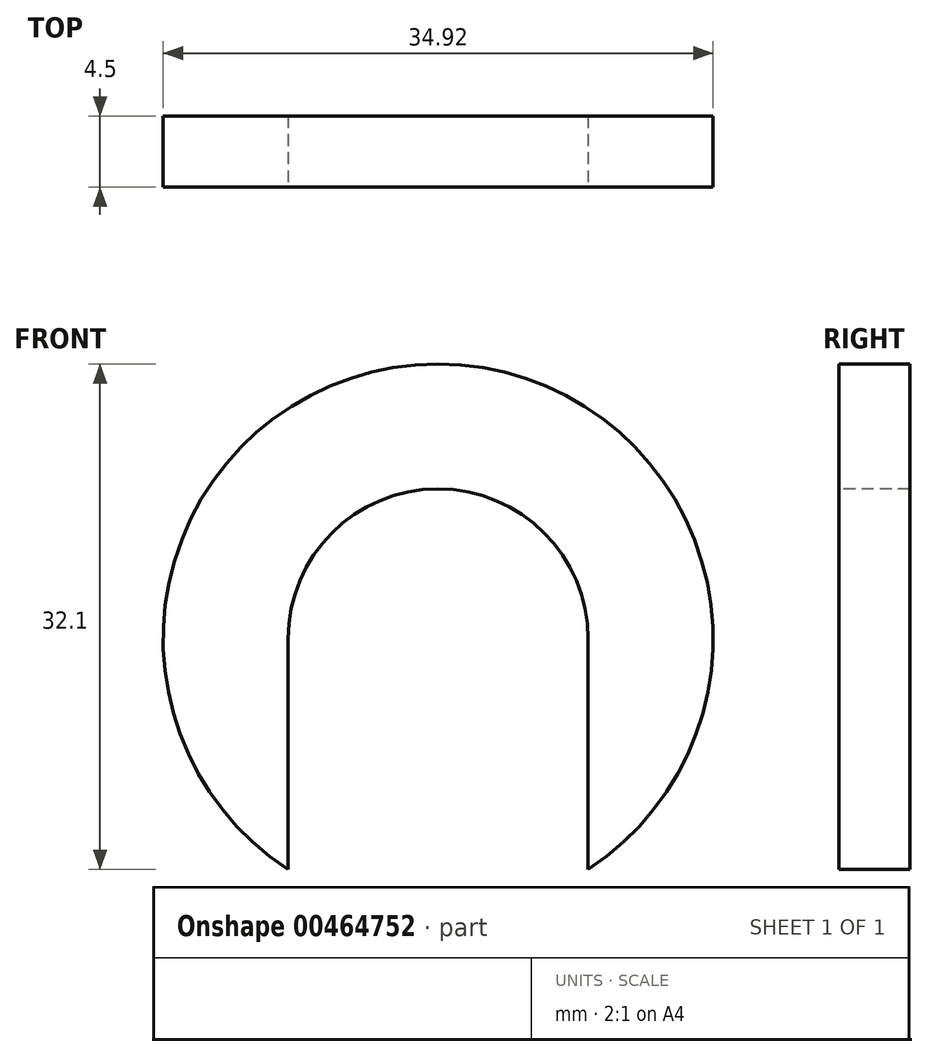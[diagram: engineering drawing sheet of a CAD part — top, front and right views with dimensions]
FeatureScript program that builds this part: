
annotation { "Feature Type Name" : "Feature", "Feature Type Description" : "" }
export const myFeature = defineFeature(function(context is Context, id is Id, definition is map)
    precondition{}
    {
        {
            var Q0;
            Q0=qCreatedBy(makeId("Front.planeOp"),FACE);
            var sketch = newSketch(context, id + "F0", { "sketchPlane" : qUnion([Q0])});
            skCircle(sketch, "E0", {"center": v(0, 0) * mm, "radius": 17.46 * mm});
            skSolve(sketch);
        }
        {
            var Q0;
            Q0=makeQuery(id+"F0.imprint","IMPRINT",FACE,{"disambiguationData":[TD([[makeQuery(id+"F0.imprint","IMPRINT",EDGE,{"derivedFrom":sQuery(id+"F0.wireOp",EDGE,"E0")}),1.0]])]});
            extrude(context, id + "F1", {"entities" : qUnion([Q0]), "oppositeDirection" : true, "depth" : (4 + (1 / 2)) * mm});
        }
        {
            var Q0;
            Q0=makeQuery(id+"F1.opExtrude","CAP_FACE",FACE,{"disambiguationData":[OSD([sQuery(id+"F0.wireOp",EDGE,"E0")])],"isStart":true});
            var sketch = newSketch(context, id + "F2", { "sketchPlane" : qUnion([Q0])});
            skLineSegment(sketch, "E1", {"start": v(-9.52, 0) * mm, "end": v(-9.53, -14.64) * mm});
            skArc(sketch, "E2.0", {"start": v(-9.53, -14.64) * mm, "mid": v(0, -17.46) * mm, "end": v(9.52, -14.64) * mm});
            skArc(sketch, "E3", {"start": v(-9.52, 0) * mm, "mid": v(0, 9.52) * mm, "end": v(9.52, 0) * mm});
            skLineSegment(sketch, "E4", {"start": v(9.52, 0) * mm, "end": v(9.53, -14.64) * mm});
            skSolve(sketch);
        }
        {
            var Q0;
            Q0=makeQuery(id+"F2.imprint","IMPRINT",FACE,{"disambiguationData":[TD([[makeQuery(id+"F2.imprint","IMPRINT",EDGE,{"derivedFrom":sQuery(id+"F2.wireOp",EDGE,"E1")}),1.0]])]});
            extrude(context, id + "F3", {"entities" : qUnion([Q0]), "operationType" : NewBodyOperationType.REMOVE, "oppositeDirection" : true, "depth" : 3.17 * mm});
        }
        {
            var Q0;
            Q0=makeQuery(id+"F1.opExtrude","CAP_FACE",FACE,{"disambiguationData":[OSD([sQuery(id+"F0.wireOp",EDGE,"E0")])],"isStart":false});
            var sketch = newSketch(context, id + "F4", { "sketchPlane" : qUnion([Q0])});
            skArc(sketch, "E5.0.0", {"start": v(-9.53, -14.64) * mm, "mid": v(0, -17.46) * mm, "end": v(9.52, -14.64) * mm});
            skLineSegment(sketch, "E6", {"start": v(-9.52, 0) * mm, "end": v(-9.53, -14.64) * mm});
            skArc(sketch, "E7", {"start": v(-9.52, 0) * mm, "mid": v(0, 9.52) * mm, "end": v(9.52, 0) * mm});
            skLineSegment(sketch, "E8", {"start": v(9.52, 0) * mm, "end": v(9.53, -14.64) * mm});
            skSolve(sketch);
        }
        {
            var Q0;
            Q0=makeQuery(id+"F4.imprint","IMPRINT",FACE,{"disambiguationData":[TD([[makeQuery(id+"F4.imprint","IMPRINT",EDGE,{"derivedFrom":sQuery(id+"F4.wireOp",EDGE,"E5.0.0")}),-1.0]])]});
            extrude(context, id + "F5", {"entities" : qUnion([Q0]), "operationType" : NewBodyOperationType.REMOVE, "oppositeDirection" : true, "depth" : 3.17 * mm});
        }
    });
